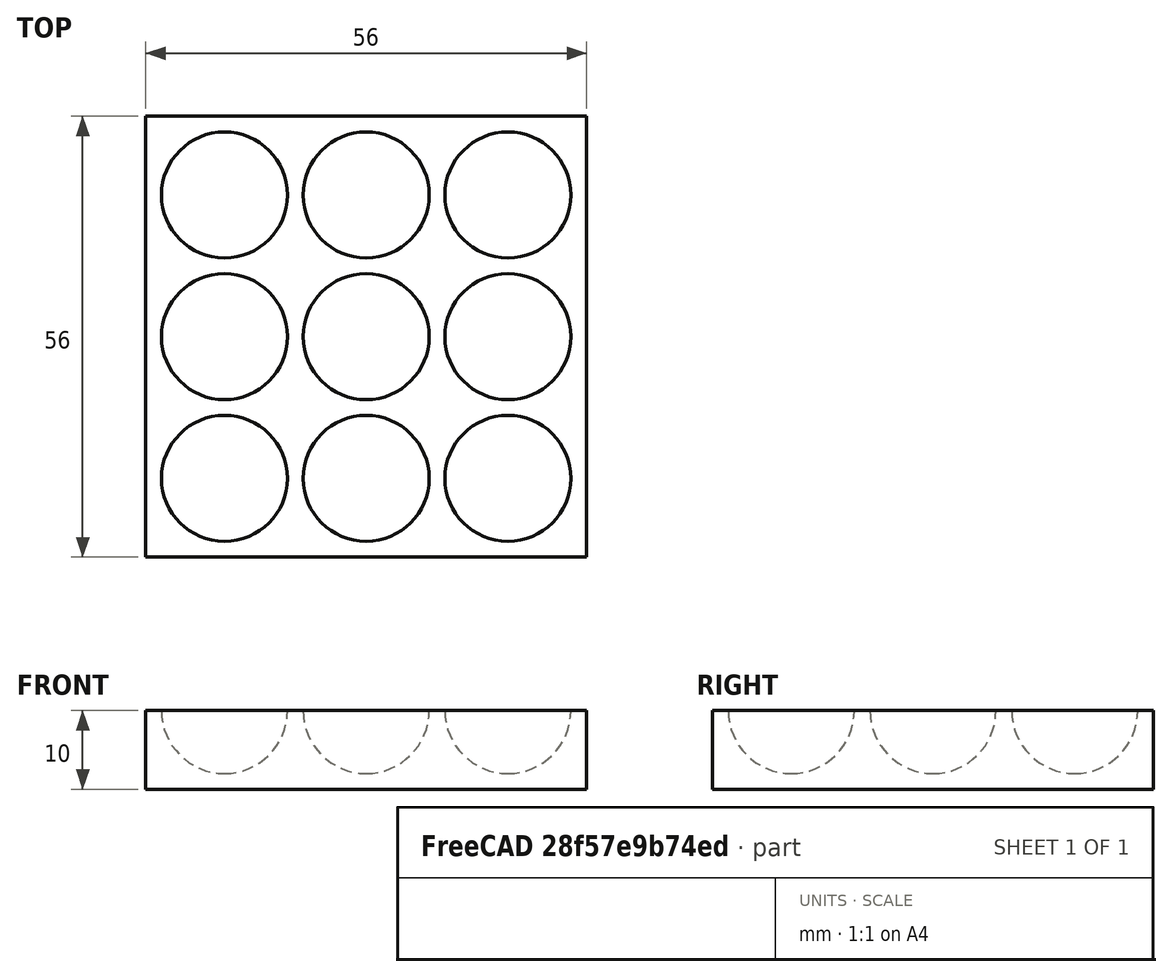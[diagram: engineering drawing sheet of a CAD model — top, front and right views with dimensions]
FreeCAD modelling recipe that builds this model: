
FCSTD DOCUMENT  (FreeCAD 1.0R39319 (Git))
Label: obj_t1_t13_e01portacaniques
License: All rights reserved
LicenseURL: https://en.wikipedia.org/wiki/All_rights_reserved
objects: Part::Sphere×1, Part::FeaturePython×1, Part::Box×1, Part::Cut×1
note: 4 computed .brp shape members not serialized (recipe doc carries the construction recipe); baked Part::Feature solids carry a one-line shape summary decoded from their .brp

FEATURE [Part::Sphere] Sphere  label="Esfera"
  Angle1 = -90
  Angle2 = 90
  Angle3 = 360
  AttacherType = Attacher::AttachEngine3D
  Radius = 8
FEATURE [Part::FeaturePython] Array  # Draft array (typed FeaturePython)
  Angle = 360
  ArrayType = 0
  Axis = (0,0,1)
  Base = -> Sphere
  Center = (0,0,0)
  Count = 9
  Fuse = false
  IntervalAxis = (0,0,0)
  IntervalX = (18,0,0)
  IntervalY = (0,18,0)
  IntervalZ = (0,0,100)
  NumberCircles = 3
  NumberPolar = 5
  NumberX = 3
  NumberY = 3
  NumberZ = 1
  Placement = pos=(10,10,10) rot=(0,0,1;0rad)
  RadialDistance = 50
  Symmetry = 1
  TangentialDistance = 25
FEATURE [Part::Box] Box  label="Cub"
  AttacherType = Attacher::AttachEngine3D
  Height = 10
  Length = 56
  Width = 56
FEATURE [Part::Cut] Cut
  Base = -> Box
  Tool = -> Array
